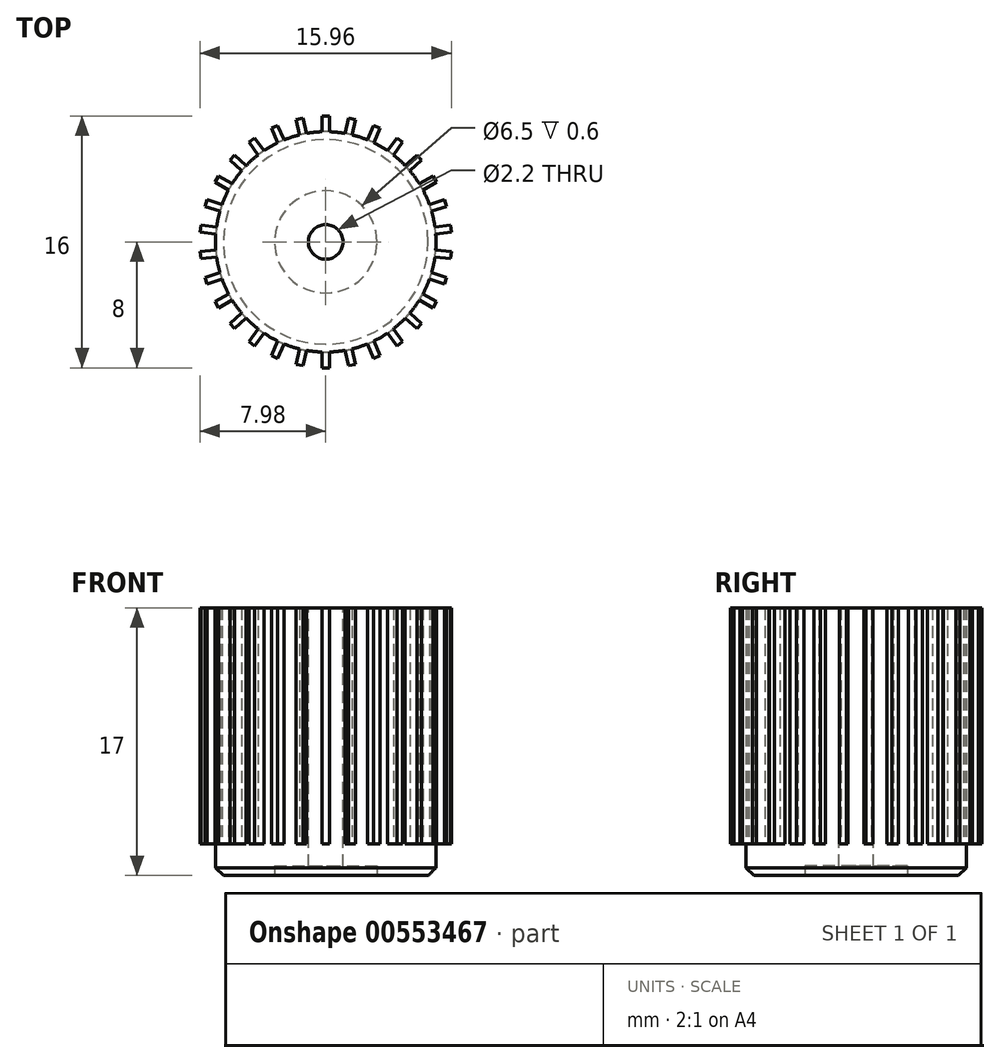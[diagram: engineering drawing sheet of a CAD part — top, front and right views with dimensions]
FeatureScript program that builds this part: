
annotation { "Feature Type Name" : "Feature", "Feature Type Description" : "" }
export const myFeature = defineFeature(function(context is Context, id is Id, definition is map)
    precondition{}
    {
        {
            var Q0;
            Q0=qCreatedBy(makeId("Top.planeOp"),FACE);
            var sketch = newSketch(context, id + "F0", { "sketchPlane" : qUnion([Q0])});
            skCircle(sketch, "E0", {"center": v(0, 0) * mm, "radius": 7 * mm});
            skSolve(sketch);
        }
        {
            var Q0;
            Q0 = qSketchRegion(id + "F0", true);
            extrude(context, id + "F1", {"entities" : qUnion([Q0]), "depth" : 15 * mm, "offsetDistance" : 25 * mm});
        }
        {
            var Q0;
            Q0=qCreatedBy(makeId("Top.planeOp"),FACE);
            var sketch = newSketch(context, id + "F2", { "sketchPlane" : qUnion([Q0])});
            skArc(sketch, "E1.0", {"start": v(0.22, 7) * mm, "mid": v(0, 7) * mm, "end": v(-0.23, 7) * mm});
            skLineSegment(sketch, "E2", {"start": v(-0.23, 7) * mm, "end": v(-0.23, 8) * mm});
            skLineSegment(sketch, "E3", {"start": v(-0.23, 8) * mm, "end": v(0.23, 8) * mm});
            skLineSegment(sketch, "E4", {"start": v(0.22, 8) * mm, "end": v(0.22, 7) * mm});
            skSolve(sketch);
        }
        {
            var Q0;
            Q0 = qSketchRegion(id + "F2", true);
            extrude(context, id + "F3", {"entities" : qUnion([Q0]), "depth" : 15 * mm, "offsetDistance" : 25 * mm});
        }
        {
            var Q0;
            Q0=makeQuery(id+"F3.opExtrude","SWEPT_BODY",BODY,{"disambiguationData":[OSD([sQuery(id+"F2.wireOp",EDGE,"E1.0"),sQuery(id+"F2.wireOp",EDGE,"E2"),sQuery(id+"F2.wireOp",EDGE,"E3"),sQuery(id+"F2.wireOp",EDGE,"E4")])]});
            var Q1;
            Q1=makeQuery(id+"F1.opExtrude","CAP_EDGE",EDGE,{"disambiguationData":[OSD([sQuery(id+"F0.wireOp",EDGE,"E0")])],"isStart":false});
            circularPattern(context, id + "F4", {"entities" : qUnion([Q0]), "axis" : qUnion([Q1]), "angle" : 360 * degree, "instanceCount" : 30, "equalSpace" : true});
        }
        {
            var Q0;
            Q0=makeQuery(id+"F4.opPattern","COPY",BODY,{"derivedFrom":makeQuery(id+"F3.opExtrude","SWEPT_BODY",BODY,{"disambiguationData":[OSD([sQuery(id+"F2.wireOp",EDGE,"E1.0"),sQuery(id+"F2.wireOp",EDGE,"E2"),sQuery(id+"F2.wireOp",EDGE,"E3"),sQuery(id+"F2.wireOp",EDGE,"E4")])]}),"instanceName":"4"});
            var Q1;
            Q1=makeQuery(id+"F4.opPattern","COPY",BODY,{"derivedFrom":makeQuery(id+"F3.opExtrude","SWEPT_BODY",BODY,{"disambiguationData":[OSD([sQuery(id+"F2.wireOp",EDGE,"E1.0"),sQuery(id+"F2.wireOp",EDGE,"E2"),sQuery(id+"F2.wireOp",EDGE,"E3"),sQuery(id+"F2.wireOp",EDGE,"E4")])]}),"instanceName":"2"});
            var Q2;
            Q2=makeQuery(id+"F4.opPattern","COPY",BODY,{"derivedFrom":makeQuery(id+"F3.opExtrude","SWEPT_BODY",BODY,{"disambiguationData":[OSD([sQuery(id+"F2.wireOp",EDGE,"E1.0"),sQuery(id+"F2.wireOp",EDGE,"E2"),sQuery(id+"F2.wireOp",EDGE,"E3"),sQuery(id+"F2.wireOp",EDGE,"E4")])]}),"instanceName":"11"});
            var Q3;
            Q3=makeQuery(id+"F4.opPattern","COPY",BODY,{"derivedFrom":makeQuery(id+"F3.opExtrude","SWEPT_BODY",BODY,{"disambiguationData":[OSD([sQuery(id+"F2.wireOp",EDGE,"E1.0"),sQuery(id+"F2.wireOp",EDGE,"E2"),sQuery(id+"F2.wireOp",EDGE,"E3"),sQuery(id+"F2.wireOp",EDGE,"E4")])]}),"instanceName":"1"});
            var Q4;
            Q4=makeQuery(id+"F4.opPattern","COPY",BODY,{"derivedFrom":makeQuery(id+"F3.opExtrude","SWEPT_BODY",BODY,{"disambiguationData":[OSD([sQuery(id+"F2.wireOp",EDGE,"E1.0"),sQuery(id+"F2.wireOp",EDGE,"E2"),sQuery(id+"F2.wireOp",EDGE,"E3"),sQuery(id+"F2.wireOp",EDGE,"E4")])]}),"instanceName":"3"});
            var Q5;
            Q5=makeQuery(id+"F4.opPattern","COPY",BODY,{"derivedFrom":makeQuery(id+"F3.opExtrude","SWEPT_BODY",BODY,{"disambiguationData":[OSD([sQuery(id+"F2.wireOp",EDGE,"E1.0"),sQuery(id+"F2.wireOp",EDGE,"E2"),sQuery(id+"F2.wireOp",EDGE,"E3"),sQuery(id+"F2.wireOp",EDGE,"E4")])]}),"instanceName":"6"});
            var Q6;
            Q6=makeQuery(id+"F3.opExtrude","SWEPT_BODY",BODY,{"disambiguationData":[OSD([sQuery(id+"F2.wireOp",EDGE,"E1.0"),sQuery(id+"F2.wireOp",EDGE,"E2"),sQuery(id+"F2.wireOp",EDGE,"E3"),sQuery(id+"F2.wireOp",EDGE,"E4")])]});
            var Q7;
            Q7=makeQuery(id+"F4.opPattern","COPY",BODY,{"derivedFrom":makeQuery(id+"F3.opExtrude","SWEPT_BODY",BODY,{"disambiguationData":[OSD([sQuery(id+"F2.wireOp",EDGE,"E1.0"),sQuery(id+"F2.wireOp",EDGE,"E2"),sQuery(id+"F2.wireOp",EDGE,"E3"),sQuery(id+"F2.wireOp",EDGE,"E4")])]}),"instanceName":"13"});
            var Q8;
            Q8=makeQuery(id+"F4.opPattern","COPY",BODY,{"derivedFrom":makeQuery(id+"F3.opExtrude","SWEPT_BODY",BODY,{"disambiguationData":[OSD([sQuery(id+"F2.wireOp",EDGE,"E1.0"),sQuery(id+"F2.wireOp",EDGE,"E2"),sQuery(id+"F2.wireOp",EDGE,"E3"),sQuery(id+"F2.wireOp",EDGE,"E4")])]}),"instanceName":"8"});
            var Q9;
            Q9=makeQuery(id+"F4.opPattern","COPY",BODY,{"derivedFrom":makeQuery(id+"F3.opExtrude","SWEPT_BODY",BODY,{"disambiguationData":[OSD([sQuery(id+"F2.wireOp",EDGE,"E1.0"),sQuery(id+"F2.wireOp",EDGE,"E2"),sQuery(id+"F2.wireOp",EDGE,"E3"),sQuery(id+"F2.wireOp",EDGE,"E4")])]}),"instanceName":"7"});
            var Q10;
            Q10=makeQuery(id+"F4.opPattern","COPY",BODY,{"derivedFrom":makeQuery(id+"F3.opExtrude","SWEPT_BODY",BODY,{"disambiguationData":[OSD([sQuery(id+"F2.wireOp",EDGE,"E1.0"),sQuery(id+"F2.wireOp",EDGE,"E2"),sQuery(id+"F2.wireOp",EDGE,"E3"),sQuery(id+"F2.wireOp",EDGE,"E4")])]}),"instanceName":"5"});
            var Q11;
            Q11=makeQuery(id+"F4.opPattern","COPY",BODY,{"derivedFrom":makeQuery(id+"F3.opExtrude","SWEPT_BODY",BODY,{"disambiguationData":[OSD([sQuery(id+"F2.wireOp",EDGE,"E1.0"),sQuery(id+"F2.wireOp",EDGE,"E2"),sQuery(id+"F2.wireOp",EDGE,"E3"),sQuery(id+"F2.wireOp",EDGE,"E4")])]}),"instanceName":"9"});
            var Q12;
            Q12=makeQuery(id+"F1.opExtrude","SWEPT_BODY",BODY,{"disambiguationData":[OSD([sQuery(id+"F0.wireOp",EDGE,"E0")])]});
            var Q13;
            Q13=makeQuery(id+"F4.opPattern","COPY",BODY,{"derivedFrom":makeQuery(id+"F3.opExtrude","SWEPT_BODY",BODY,{"disambiguationData":[OSD([sQuery(id+"F2.wireOp",EDGE,"E1.0"),sQuery(id+"F2.wireOp",EDGE,"E2"),sQuery(id+"F2.wireOp",EDGE,"E3"),sQuery(id+"F2.wireOp",EDGE,"E4")])]}),"instanceName":"10"});
            var Q14;
            Q14=makeQuery(id+"F4.opPattern","COPY",BODY,{"derivedFrom":makeQuery(id+"F3.opExtrude","SWEPT_BODY",BODY,{"disambiguationData":[OSD([sQuery(id+"F2.wireOp",EDGE,"E1.0"),sQuery(id+"F2.wireOp",EDGE,"E2"),sQuery(id+"F2.wireOp",EDGE,"E3"),sQuery(id+"F2.wireOp",EDGE,"E4")])]}),"instanceName":"14"});
            var Q15;
            Q15=makeQuery(id+"F4.opPattern","COPY",BODY,{"derivedFrom":makeQuery(id+"F3.opExtrude","SWEPT_BODY",BODY,{"disambiguationData":[OSD([sQuery(id+"F2.wireOp",EDGE,"E1.0"),sQuery(id+"F2.wireOp",EDGE,"E2"),sQuery(id+"F2.wireOp",EDGE,"E3"),sQuery(id+"F2.wireOp",EDGE,"E4")])]}),"instanceName":"12"});
            var Q16;
            Q16=makeQuery(id+"F4.opPattern","COPY",BODY,{"derivedFrom":makeQuery(id+"F3.opExtrude","SWEPT_BODY",BODY,{"disambiguationData":[OSD([sQuery(id+"F2.wireOp",EDGE,"E1.0"),sQuery(id+"F2.wireOp",EDGE,"E2"),sQuery(id+"F2.wireOp",EDGE,"E3"),sQuery(id+"F2.wireOp",EDGE,"E4")])]}),"instanceName":"18"});
            var Q17;
            Q17=makeQuery(id+"F4.opPattern","COPY",BODY,{"derivedFrom":makeQuery(id+"F3.opExtrude","SWEPT_BODY",BODY,{"disambiguationData":[OSD([sQuery(id+"F2.wireOp",EDGE,"E1.0"),sQuery(id+"F2.wireOp",EDGE,"E2"),sQuery(id+"F2.wireOp",EDGE,"E3"),sQuery(id+"F2.wireOp",EDGE,"E4")])]}),"instanceName":"17"});
            var Q18;
            Q18=makeQuery(id+"F4.opPattern","COPY",BODY,{"derivedFrom":makeQuery(id+"F3.opExtrude","SWEPT_BODY",BODY,{"disambiguationData":[OSD([sQuery(id+"F2.wireOp",EDGE,"E1.0"),sQuery(id+"F2.wireOp",EDGE,"E2"),sQuery(id+"F2.wireOp",EDGE,"E3"),sQuery(id+"F2.wireOp",EDGE,"E4")])]}),"instanceName":"16"});
            var Q19;
            Q19=makeQuery(id+"F4.opPattern","COPY",BODY,{"derivedFrom":makeQuery(id+"F3.opExtrude","SWEPT_BODY",BODY,{"disambiguationData":[OSD([sQuery(id+"F2.wireOp",EDGE,"E1.0"),sQuery(id+"F2.wireOp",EDGE,"E2"),sQuery(id+"F2.wireOp",EDGE,"E3"),sQuery(id+"F2.wireOp",EDGE,"E4")])]}),"instanceName":"15"});
            var Q20;
            Q20=makeQuery(id+"F4.opPattern","COPY",BODY,{"derivedFrom":makeQuery(id+"F3.opExtrude","SWEPT_BODY",BODY,{"disambiguationData":[OSD([sQuery(id+"F2.wireOp",EDGE,"E1.0"),sQuery(id+"F2.wireOp",EDGE,"E2"),sQuery(id+"F2.wireOp",EDGE,"E3"),sQuery(id+"F2.wireOp",EDGE,"E4")])]}),"instanceName":"19"});
            var Q21;
            Q21=makeQuery(id+"F4.opPattern","COPY",BODY,{"derivedFrom":makeQuery(id+"F3.opExtrude","SWEPT_BODY",BODY,{"disambiguationData":[OSD([sQuery(id+"F2.wireOp",EDGE,"E1.0"),sQuery(id+"F2.wireOp",EDGE,"E2"),sQuery(id+"F2.wireOp",EDGE,"E3"),sQuery(id+"F2.wireOp",EDGE,"E4")])]}),"instanceName":"20"});
            var Q22;
            Q22=makeQuery(id+"F4.opPattern","COPY",BODY,{"derivedFrom":makeQuery(id+"F3.opExtrude","SWEPT_BODY",BODY,{"disambiguationData":[OSD([sQuery(id+"F2.wireOp",EDGE,"E1.0"),sQuery(id+"F2.wireOp",EDGE,"E2"),sQuery(id+"F2.wireOp",EDGE,"E3"),sQuery(id+"F2.wireOp",EDGE,"E4")])]}),"instanceName":"21"});
            var Q23;
            Q23=makeQuery(id+"F4.opPattern","COPY",BODY,{"derivedFrom":makeQuery(id+"F3.opExtrude","SWEPT_BODY",BODY,{"disambiguationData":[OSD([sQuery(id+"F2.wireOp",EDGE,"E1.0"),sQuery(id+"F2.wireOp",EDGE,"E2"),sQuery(id+"F2.wireOp",EDGE,"E3"),sQuery(id+"F2.wireOp",EDGE,"E4")])]}),"instanceName":"22"});
            var Q24;
            Q24=makeQuery(id+"F4.opPattern","COPY",BODY,{"derivedFrom":makeQuery(id+"F3.opExtrude","SWEPT_BODY",BODY,{"disambiguationData":[OSD([sQuery(id+"F2.wireOp",EDGE,"E1.0"),sQuery(id+"F2.wireOp",EDGE,"E2"),sQuery(id+"F2.wireOp",EDGE,"E3"),sQuery(id+"F2.wireOp",EDGE,"E4")])]}),"instanceName":"23"});
            var Q25;
            Q25=makeQuery(id+"F4.opPattern","COPY",BODY,{"derivedFrom":makeQuery(id+"F3.opExtrude","SWEPT_BODY",BODY,{"disambiguationData":[OSD([sQuery(id+"F2.wireOp",EDGE,"E1.0"),sQuery(id+"F2.wireOp",EDGE,"E2"),sQuery(id+"F2.wireOp",EDGE,"E3"),sQuery(id+"F2.wireOp",EDGE,"E4")])]}),"instanceName":"24"});
            var Q26;
            Q26=makeQuery(id+"F4.opPattern","COPY",BODY,{"derivedFrom":makeQuery(id+"F3.opExtrude","SWEPT_BODY",BODY,{"disambiguationData":[OSD([sQuery(id+"F2.wireOp",EDGE,"E1.0"),sQuery(id+"F2.wireOp",EDGE,"E2"),sQuery(id+"F2.wireOp",EDGE,"E3"),sQuery(id+"F2.wireOp",EDGE,"E4")])]}),"instanceName":"25"});
            var Q27;
            Q27=makeQuery(id+"F4.opPattern","COPY",BODY,{"derivedFrom":makeQuery(id+"F3.opExtrude","SWEPT_BODY",BODY,{"disambiguationData":[OSD([sQuery(id+"F2.wireOp",EDGE,"E1.0"),sQuery(id+"F2.wireOp",EDGE,"E2"),sQuery(id+"F2.wireOp",EDGE,"E3"),sQuery(id+"F2.wireOp",EDGE,"E4")])]}),"instanceName":"26"});
            var Q28;
            Q28=makeQuery(id+"F4.opPattern","COPY",BODY,{"derivedFrom":makeQuery(id+"F3.opExtrude","SWEPT_BODY",BODY,{"disambiguationData":[OSD([sQuery(id+"F2.wireOp",EDGE,"E1.0"),sQuery(id+"F2.wireOp",EDGE,"E2"),sQuery(id+"F2.wireOp",EDGE,"E3"),sQuery(id+"F2.wireOp",EDGE,"E4")])]}),"instanceName":"27"});
            var Q29;
            Q29=makeQuery(id+"F4.opPattern","COPY",BODY,{"derivedFrom":makeQuery(id+"F3.opExtrude","SWEPT_BODY",BODY,{"disambiguationData":[OSD([sQuery(id+"F2.wireOp",EDGE,"E1.0"),sQuery(id+"F2.wireOp",EDGE,"E2"),sQuery(id+"F2.wireOp",EDGE,"E3"),sQuery(id+"F2.wireOp",EDGE,"E4")])]}),"instanceName":"28"});
            var Q30;
            Q30=makeQuery(id+"F4.opPattern","COPY",BODY,{"derivedFrom":makeQuery(id+"F3.opExtrude","SWEPT_BODY",BODY,{"disambiguationData":[OSD([sQuery(id+"F2.wireOp",EDGE,"E1.0"),sQuery(id+"F2.wireOp",EDGE,"E2"),sQuery(id+"F2.wireOp",EDGE,"E3"),sQuery(id+"F2.wireOp",EDGE,"E4")])]}),"instanceName":"29"});
            booleanBodies(context, id + "F5", {"operationType" : BooleanOperationType.UNION, "tools" : qUnion([Q0, Q1, Q2, Q3, Q4, Q5, Q6, Q7, Q8, Q9, Q10, Q11, Q12, Q13, Q14, Q15, Q16, Q17, Q18, Q19, Q20, Q21, Q22, Q23, Q24, Q25, Q26, Q27, Q28, Q29, Q30])});
        }
        {
            var Q0;
            Q0=qCreatedBy(makeId("Top.planeOp"),FACE);
            var sketch = newSketch(context, id + "F6", { "sketchPlane" : qUnion([Q0])});
            skCircle(sketch, "E5", {"center": v(0, 0) * mm, "radius": 7 * mm});
            skSolve(sketch);
        }
        {
            var Q0;
            Q0 = qSketchRegion(id + "F6", true);
            extrude(context, id + "F7", {"entities" : qUnion([Q0]), "operationType" : NewBodyOperationType.ADD, "oppositeDirection" : true, "depth" : 2 * mm, "offsetDistance" : 25 * mm});
        }
        {
            var Q0;
            Q0=makeQuery(id+"F7.opExtrude","CAP_EDGE",EDGE,{"disambiguationData":[OSD([sQuery(id+"F6.wireOp",EDGE,"E5")])],"isStart":false});
            chamfer(context, id + "F8", {"entities" : qUnion([Q0]), "width" : 0.5 * mm, "tangentPropagation" : true});
        }
        {
            var Q0;
            Q0=makeQuery(id+"F7.opExtrude","CAP_FACE",FACE,{"disambiguationData":[OSD([sQuery(id+"F6.wireOp",EDGE,"E5")])],"isStart":false});
            var sketch = newSketch(context, id + "F9", { "sketchPlane" : qUnion([Q0])});
            skCircle(sketch, "E6", {"center": v(0, 0) * mm, "radius": 3.25 * mm});
            skSolve(sketch);
        }
        {
            var Q0;
            Q0 = qSketchRegion(id + "F9", true);
            extrude(context, id + "F10", {"entities" : qUnion([Q0]), "operationType" : NewBodyOperationType.REMOVE, "oppositeDirection" : true, "depth" : 0.6 * mm, "offsetDistance" : 25 * mm});
        }
        {
            var Q0;
            Q0=makeQuery(id+"F10.boolean.opBoolean","COPY",FACE,{"derivedFrom":makeQuery(id+"F10.opExtrude","CAP_FACE",FACE,{"disambiguationData":[OSD([sQuery(id+"F9.wireOp",EDGE,"E6")])],"isStart":false})});
            var sketch = newSketch(context, id + "F11", { "sketchPlane" : qUnion([Q0])});
            skCircle(sketch, "E7", {"center": v(0, 0) * mm, "radius": 1 * mm});
            skSolve(sketch);
        }
        {
            var Q0;
            {var subQ0=makeQuery(id+"F3.opExtrude","CAP_FACE",FACE,{"disambiguationData":[OSD([sQuery(id+"F2.wireOp",EDGE,"E1.0"),sQuery(id+"F2.wireOp",EDGE,"E2"),sQuery(id+"F2.wireOp",EDGE,"E3"),sQuery(id+"F2.wireOp",EDGE,"E4")])],"isStart":false});Q0=makeQuery(id+"F5.opBoolean","MERGE",FACE,{"derivedFrom":[makeQuery(id+"F1.opExtrude","CAP_FACE",FACE,{"disambiguationData":[OSD([sQuery(id+"F0.wireOp",EDGE,"E0")])],"isStart":false}),subQ0,makeQuery(id+"F4.opPattern","COPY",FACE,{"derivedFrom":subQ0,"instanceName":"1"}),makeQuery(id+"F4.opPattern","COPY",FACE,{"derivedFrom":subQ0,"instanceName":"2"}),makeQuery(id+"F4.opPattern","COPY",FACE,{"derivedFrom":subQ0,"instanceName":"3"}),makeQuery(id+"F4.opPattern","COPY",FACE,{"derivedFrom":subQ0,"instanceName":"4"}),makeQuery(id+"F4.opPattern","COPY",FACE,{"derivedFrom":subQ0,"instanceName":"5"}),makeQuery(id+"F4.opPattern","COPY",FACE,{"derivedFrom":subQ0,"instanceName":"6"}),makeQuery(id+"F4.opPattern","COPY",FACE,{"derivedFrom":subQ0,"instanceName":"7"}),makeQuery(id+"F4.opPattern","COPY",FACE,{"derivedFrom":subQ0,"instanceName":"8"}),makeQuery(id+"F4.opPattern","COPY",FACE,{"derivedFrom":subQ0,"instanceName":"9"}),makeQuery(id+"F4.opPattern","COPY",FACE,{"derivedFrom":subQ0,"instanceName":"10"}),makeQuery(id+"F4.opPattern","COPY",FACE,{"derivedFrom":subQ0,"instanceName":"11"}),makeQuery(id+"F4.opPattern","COPY",FACE,{"derivedFrom":subQ0,"instanceName":"12"}),makeQuery(id+"F4.opPattern","COPY",FACE,{"derivedFrom":subQ0,"instanceName":"13"}),makeQuery(id+"F4.opPattern","COPY",FACE,{"derivedFrom":subQ0,"instanceName":"14"}),makeQuery(id+"F4.opPattern","COPY",FACE,{"derivedFrom":subQ0,"instanceName":"15"}),makeQuery(id+"F4.opPattern","COPY",FACE,{"derivedFrom":subQ0,"instanceName":"16"}),makeQuery(id+"F4.opPattern","COPY",FACE,{"derivedFrom":subQ0,"instanceName":"17"}),makeQuery(id+"F4.opPattern","COPY",FACE,{"derivedFrom":subQ0,"instanceName":"18"}),makeQuery(id+"F4.opPattern","COPY",FACE,{"derivedFrom":subQ0,"instanceName":"19"}),makeQuery(id+"F4.opPattern","COPY",FACE,{"derivedFrom":subQ0,"instanceName":"20"}),makeQuery(id+"F4.opPattern","COPY",FACE,{"derivedFrom":subQ0,"instanceName":"21"}),makeQuery(id+"F4.opPattern","COPY",FACE,{"derivedFrom":subQ0,"instanceName":"22"}),makeQuery(id+"F4.opPattern","COPY",FACE,{"derivedFrom":subQ0,"instanceName":"23"}),makeQuery(id+"F4.opPattern","COPY",FACE,{"derivedFrom":subQ0,"instanceName":"24"}),makeQuery(id+"F4.opPattern","COPY",FACE,{"derivedFrom":subQ0,"instanceName":"25"}),makeQuery(id+"F4.opPattern","COPY",FACE,{"derivedFrom":subQ0,"instanceName":"26"}),makeQuery(id+"F4.opPattern","COPY",FACE,{"derivedFrom":subQ0,"instanceName":"27"}),makeQuery(id+"F4.opPattern","COPY",FACE,{"derivedFrom":subQ0,"instanceName":"28"}),makeQuery(id+"F4.opPattern","COPY",FACE,{"derivedFrom":subQ0,"instanceName":"29"})]});}
            var sketch = newSketch(context, id + "F12", { "sketchPlane" : qUnion([Q0])});
            skCircle(sketch, "E8", {"center": v(0, 0) * mm, "radius": 1.1 * mm});
            skSolve(sketch);
        }
        {
            var Q0;
            Q0 = qSketchRegion(id + "F12", true);
            extrude(context, id + "F13", {"entities" : qUnion([Q0]), "operationType" : NewBodyOperationType.REMOVE, "endBound" : BoundingType.SYMMETRIC, "oppositeDirection" : true, "depth" : 50 * mm, "offsetDistance" : 25 * mm});
        }
    });
